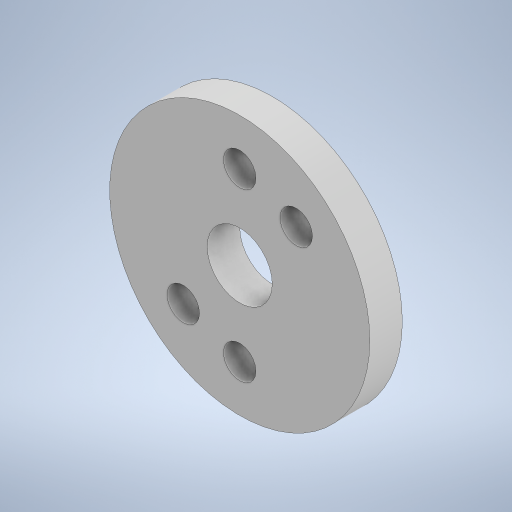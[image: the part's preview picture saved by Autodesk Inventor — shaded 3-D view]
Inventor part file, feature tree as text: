
AUTODESK INVENTOR PART (.ipt)
format: ipt  version: 2023.2 (Build 272271000, 271)  size: 252,416 bytes
history: native  units: mm
features: extrude x2, sketch x2
ambient origin geometry x8: Origin, YZ Plane, XZ Plane, XY Plane, X Axis, Y Axis, Z Axis, Center Point
bodies: Solid1 (feature_tree)
feature tree (4):
  extrude  "Extrusion1"  Depth=10.0mm
  extrude  "Extrusion2"  Depth=5.0mm
  sketch  "Sketch1"  dims[d0=40.0mm d1=10.0mm]
  sketch  "Sketch2"  dims[d2=5.0mm d3=0.0mm d4=12.85mm d5=5.0mm d6=12.85mm d8=5.0mm d9=5.0mm d10=0.0mm d15=90.0deg d17=8.290314mm d18=7.417649mm d20=12.85mm d21=23.125613mm d22=5.0mm d23=12.85mm d24=5.0mm d25=7.417649mm]
